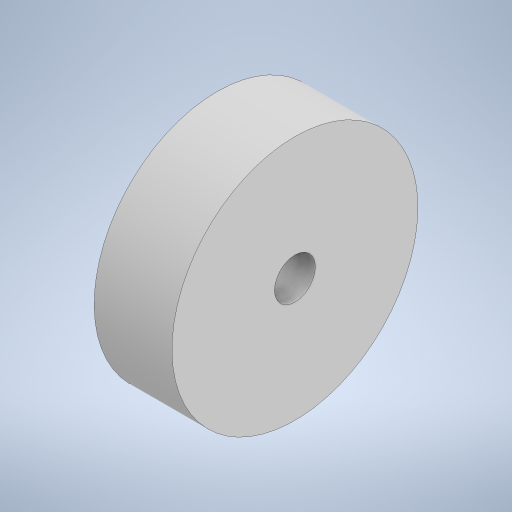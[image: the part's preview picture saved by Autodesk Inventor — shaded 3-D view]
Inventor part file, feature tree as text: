
AUTODESK INVENTOR PART (.ipt)
format: ipt  version: 2023 (Build 270158000, 158)  size: 206,336 bytes
history: native  units: mm
features: other x1, extrude x1, sketch x1
ambient origin geometry x8: Origin, YZ Plane, XZ Plane, XY Plane, X Axis, Y Axis, Z Axis, Center Point
bodies: Body1 (feature_tree)
feature tree (3):
  other  "Bryła1"
  extrude  "Wyciągnięcie proste1"  Depth=12.0mm
  sketch  "Szkic1"
